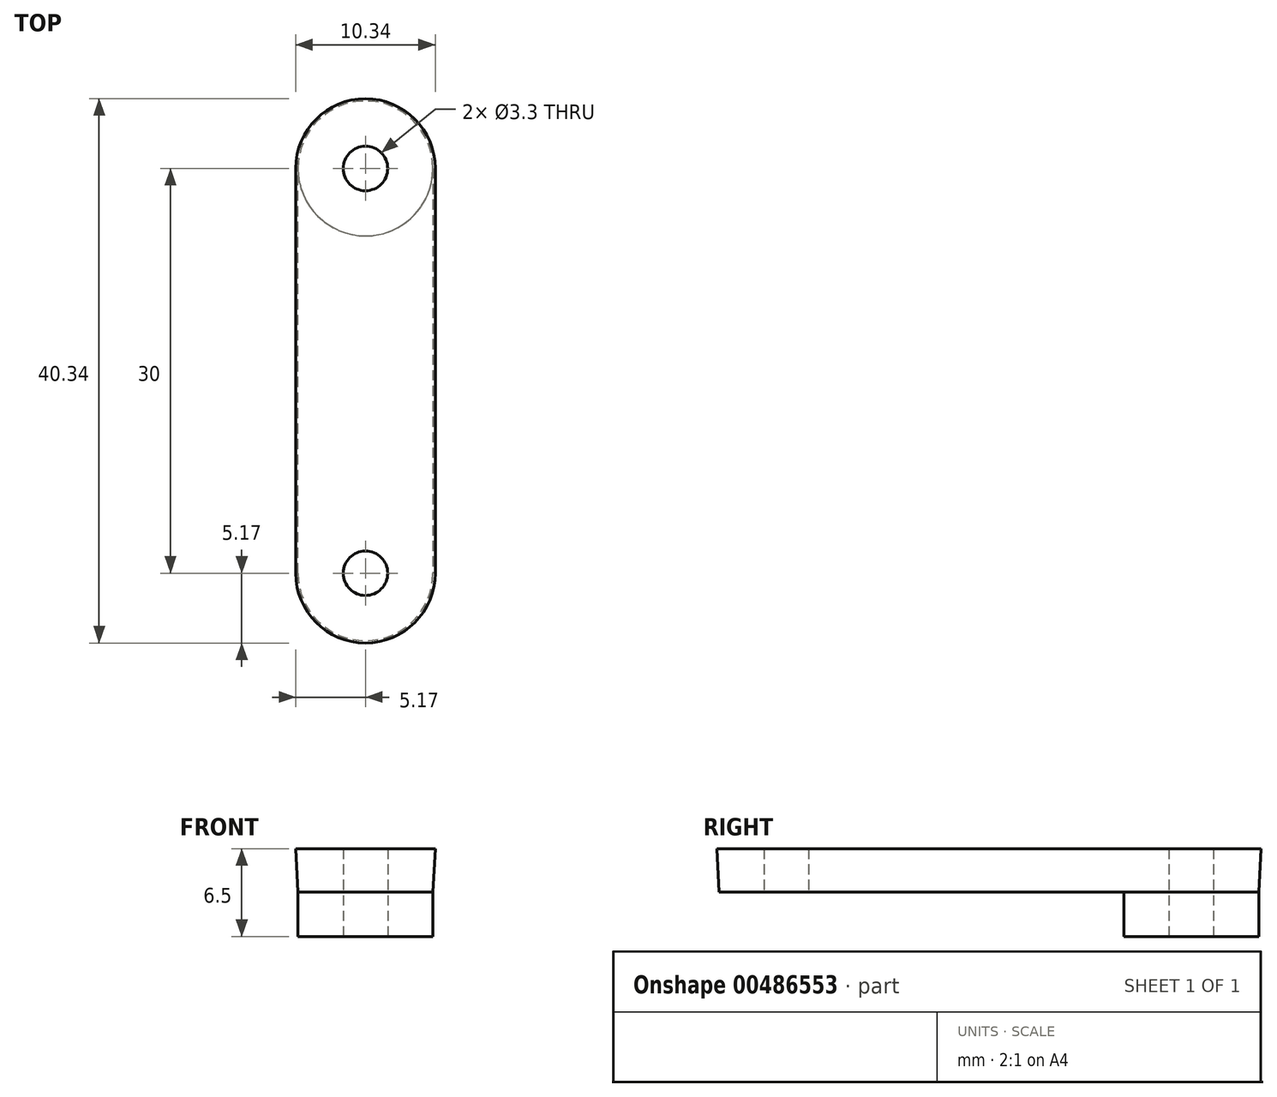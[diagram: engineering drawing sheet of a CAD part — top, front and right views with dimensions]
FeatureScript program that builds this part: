
annotation { "Feature Type Name" : "Feature", "Feature Type Description" : "" }
export const myFeature = defineFeature(function(context is Context, id is Id, definition is map)
    precondition{}
    {
        {
            var Q0;
            Q0=qCreatedBy(makeId("Top.planeOp"),FACE);
            var sketch = newSketch(context, id + "F0", { "sketchPlane" : qUnion([Q0])});
            skCircle(sketch, "E0", {"center": v(0, 0) * mm, "radius": 1.65 * mm});
            skSolve(sketch);
        }
        {
            var Q0;
            Q0=qCreatedBy(makeId("Top.planeOp"),FACE);
            var sketch = newSketch(context, id + "F1", { "sketchPlane" : qUnion([Q0])});
            skCircle(sketch, "E1", {"center": v(0, 0) * mm, "radius": 1.65 * mm});
            skCircle(sketch, "E2", {"center": v(0, 0) * mm, "radius": 5 * mm});
            skCircle(sketch, "E3", {"center": v(0, -30) * mm, "radius": 5 * mm});
            skLineSegment(sketch, "E4", {"start": v(-5, -30) * mm, "end": v(-5, 0) * mm});
            skLineSegment(sketch, "E5", {"start": v(5, 0) * mm, "end": v(5, -30) * mm});
            skSolve(sketch);
        }
        {
            var Q0;
            Q0 = qSketchRegion(id + "F1", true);
            extrude(context, id + "F2", {"entities" : qUnion([Q0]), "depth" : 3.2 * mm, "offsetDistance" : 25 * mm, "hasDraft" : true, "draftAngle" : 3 * degree});
        }
        {
            var Q0;
            Q0 = qSketchRegion(id + "F0", true);
            extrude(context, id + "F3", {"entities" : qUnion([Q0]), "operationType" : NewBodyOperationType.REMOVE, "depth" : 3.2 * mm, "offsetDistance" : 25 * mm});
        }
        {
            var Q0;
            Q0=qCreatedBy(makeId("Top.planeOp"),FACE);
            var sketch = newSketch(context, id + "F4", { "sketchPlane" : qUnion([Q0])});
            skCircle(sketch, "E6", {"center": v(0, 0) * mm, "radius": 1.65 * mm});
            skSolve(sketch);
        }
        {
            var Q0;
            Q0=qCreatedBy(makeId("Top.planeOp"),FACE);
            var sketch = newSketch(context, id + "F5", { "sketchPlane" : qUnion([Q0])});
            skCircle(sketch, "E7", {"center": v(0, 0) * mm, "radius": 5 * mm});
            skSolve(sketch);
        }
        {
            var Q0;
            Q0 = qSketchRegion(id + "F5", true);
            extrude(context, id + "F6", {"entities" : qUnion([Q0]), "operationType" : NewBodyOperationType.ADD, "oppositeDirection" : true, "depth" : 3.3 * mm, "offsetDistance" : 25 * mm});
        }
        {
            var Q0;
            Q0 = qSketchRegion(id + "F4", true);
            extrude(context, id + "F7", {"entities" : qUnion([Q0]), "operationType" : NewBodyOperationType.REMOVE, "oppositeDirection" : true, "depth" : 3.3 * mm, "offsetDistance" : 25 * mm});
        }
        {
            var Q0;
            Q0=qCreatedBy(makeId("Top.planeOp"),FACE);
            var sketch = newSketch(context, id + "F8", { "sketchPlane" : qUnion([Q0])});
            skCircle(sketch, "E8", {"center": v(0, -30) * mm, "radius": 1.65 * mm});
            skSolve(sketch);
        }
        {
            var Q0;
            Q0 = qSketchRegion(id + "F8", true);
            extrude(context, id + "F9", {"entities" : qUnion([Q0]), "operationType" : NewBodyOperationType.REMOVE, "depth" : 3.2 * mm, "offsetDistance" : 25 * mm});
        }
    });
